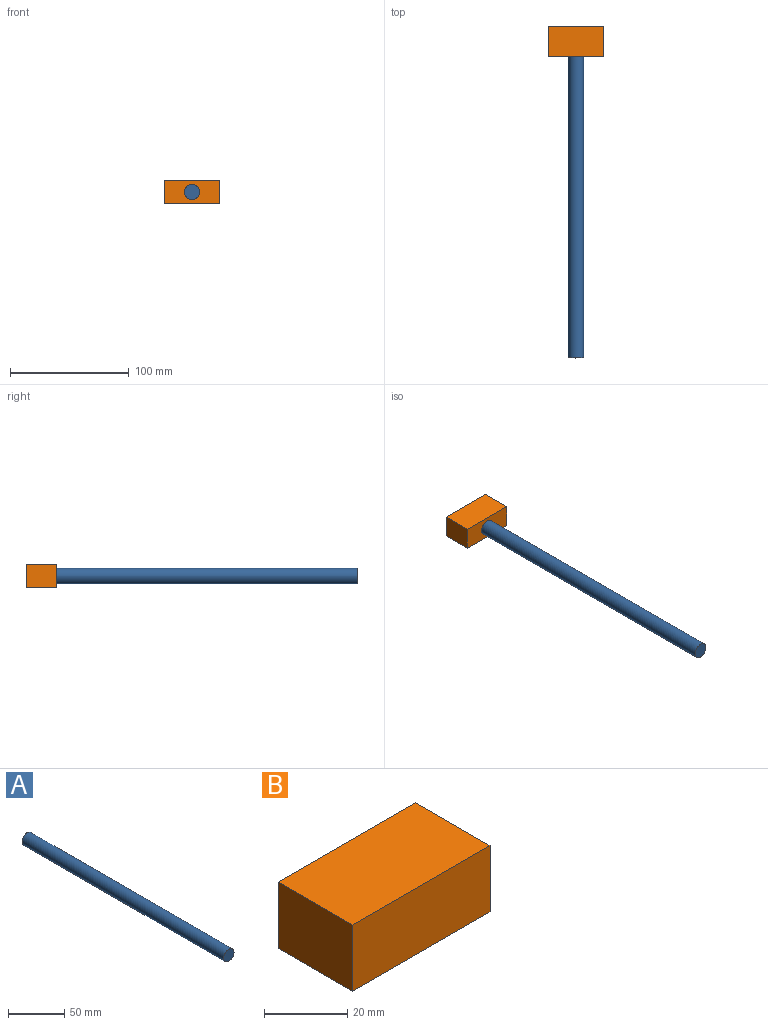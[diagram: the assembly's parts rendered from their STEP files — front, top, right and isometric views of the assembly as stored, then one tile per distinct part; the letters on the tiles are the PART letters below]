
ASSEMBLY  parts=2 mates=1
PART A: 3 faces, bbox 12.9x254x12.9 mm
  f0: cylinder r=6.46mm len=254mm, axis (0,1,0), area 10314.4mm2, adj f1,f2
  f1: plane 12.93x12.93mm, normal (0,-1,0), area 131.2mm2, adj f0
  f2: plane 12.93x12.93mm, normal (0,1,0), area 131.2mm2, adj f0
PART B: 6 faces, bbox 46.8x25.4x19.5 mm
  f0: plane 25.4x19.54mm, normal (-1,0,0), area 496.4mm2, adj f1,f3,f4,f5
  f1: plane 46.83x25.4mm, normal (0,0,-1), area 1189.4mm2, adj f0,f2,f4,f5
  f2: plane 25.4x19.54mm, normal (1,0,0), area 496.4mm2, adj f1,f3,f4,f5
  f3: plane 46.83x25.4mm, normal (0,0,1), area 1189.4mm2, adj f0,f2,f4,f5
  f4: plane 46.83x19.54mm, normal (0,-1,0), area 915.1mm2, adj f0,f1,f2,f3
  f5: plane 46.83x19.54mm, normal (0,1,0), area 915.1mm2, adj f0,f1,f2,f3
PLACE A t=(-149.14,107.49,-57.68)mm
PLACE B t=(-190.43,132.89,-102.29)mm
MATE slider B.f4 <-> A.f0  axis (0,-1,0) through (-149.14,107.49,-57.68)mm
